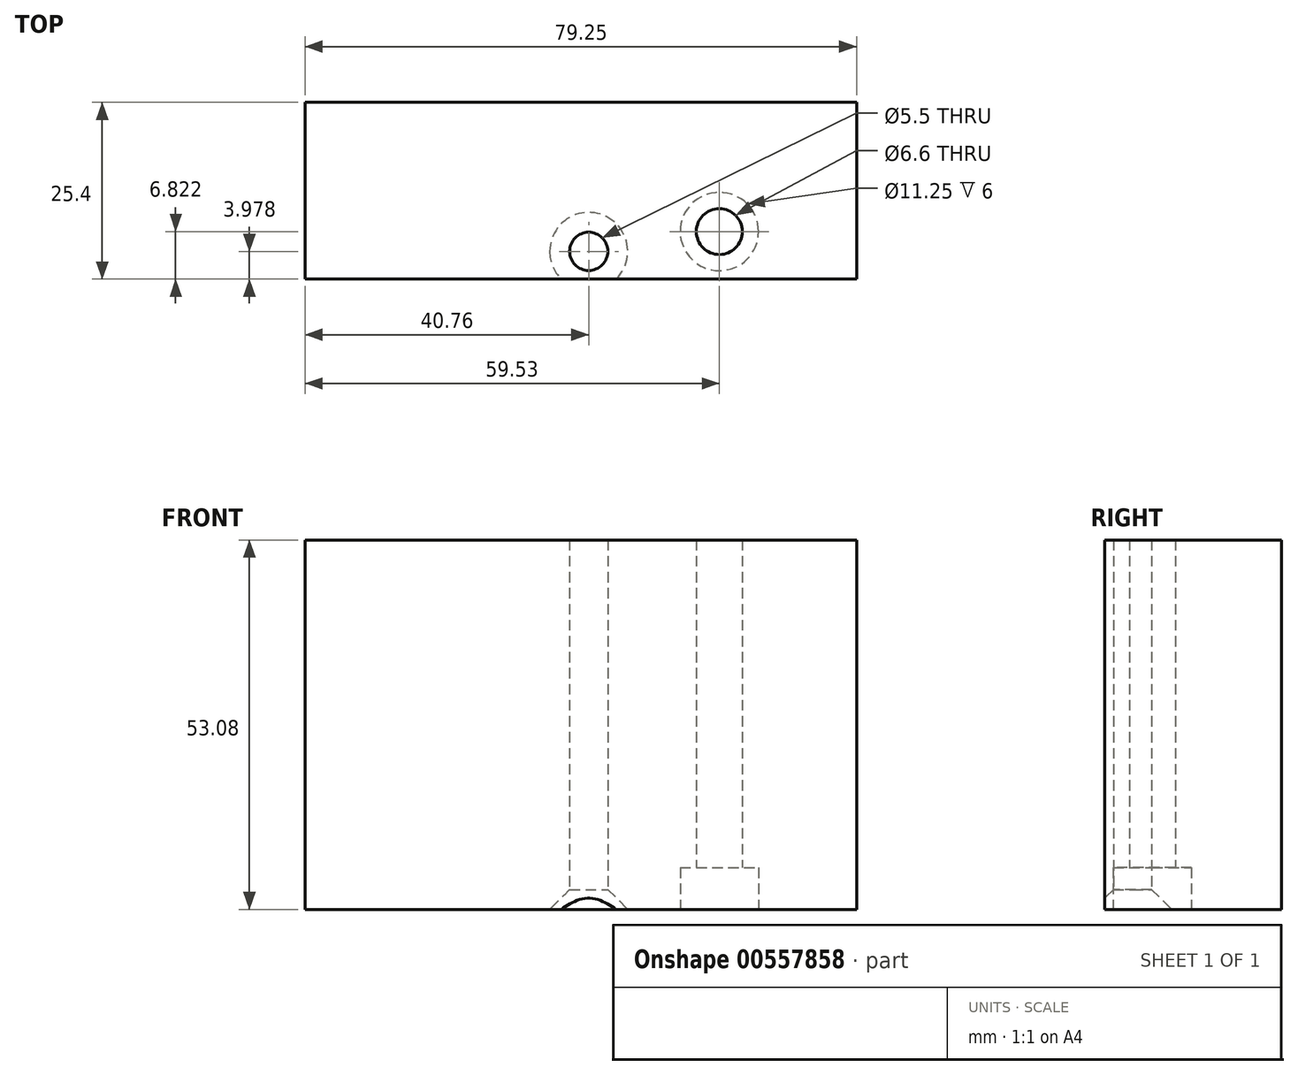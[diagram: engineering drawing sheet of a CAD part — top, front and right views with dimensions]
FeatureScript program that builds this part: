
annotation { "Feature Type Name" : "Feature", "Feature Type Description" : "" }
export const myFeature = defineFeature(function(context is Context, id is Id, definition is map)
    precondition{}
    {
        {
            var Q0;
            Q0=qCreatedBy(makeId("Front.planeOp"),FACE);
            var sketch = newSketch(context, id + "F0", { "sketchPlane" : qUnion([Q0])});
            skLineSegment(sketch, "E0.bottom", {"start": v(-21.8, 17.25) * mm, "end": v(57.45, 17.25) * mm});
            skLineSegment(sketch, "E0.top", {"start": v(-21.8, -35.83) * mm, "end": v(57.45, -35.83) * mm});
            skLineSegment(sketch, "E0.left", {"start": v(-21.8, 17.25) * mm, "end": v(-21.8, -35.83) * mm});
            skLineSegment(sketch, "E0.right", {"start": v(57.45, 17.25) * mm, "end": v(57.45, -35.83) * mm});
            skSolve(sketch);
        }
        {
            var Q0;
            Q0 = qSketchRegion(id + "F0", true);
            extrude(context, id + "F1", {"entities" : qUnion([Q0]), "endBound" : BoundingType.SYMMETRIC, "depth" : 25.4 * mm, "offsetDistance" : 25.4 * mm});
        }
        {
            var Q0;
            Q0=makeQuery(id+"F1.opExtrude","SWEPT_FACE",FACE,{"disambiguationData":[OSD([sQuery(id+"F0.wireOp",EDGE,"E0.top")])]});
            var sketch = newSketch(context, id + "F2", { "sketchPlane" : qUnion([Q0])});
            skLineSegment(sketch, "E1", {"start": v(18.96, 8.72) * mm, "end": v(18.96, 0) * mm});
            skLineSegment(sketch, "E2", {"start": v(13.46, 5.3) * mm, "end": v(36.4, 5.3) * mm});
            skSolve(sketch);
        }
        {
            var Q0;
            Q0=sQuery(id+"F2.wireOp",VERTEX,"E1.start");
            var Q1;
            Q1=makeQuery(id+"F1.opExtrude","SWEPT_BODY",BODY,{"disambiguationData":[OSD([sQuery(id+"F0.wireOp",EDGE,"E0.bottom"),sQuery(id+"F0.wireOp",EDGE,"E0.top"),sQuery(id+"F0.wireOp",EDGE,"E0.left"),sQuery(id+"F0.wireOp",EDGE,"E0.right")])]});
            hole(context, id + "F3", {"style" : HoleStyle.C_SINK, "endStyle" : HoleEndStyle.THROUGH, "standardTappedOrClearance" : lookupTablePath({ "standard" : "ISO", "fit" : "Normal", "size" : "M5", "type" : "Clearance" }), "standardBlindInLast" : lookupTablePath({ "fit" : "Standard", "standard" : "ISO", "size" : "M5", "type" : "Clearance" }), "holeDiameter" : 5.5 * mm, "cSinkDiameter" : 11.2 * mm, "cSinkAngle" : 90 * degree, "isTappedThrough" : true, "tappedDepth" : 12.7 * mm, "tapClearance" : 3, "startFromSketch" : true, "locations" : qUnion([Q0]), "scope" : qUnion([Q1])});
        }
        {
            var Q0;
            Q0=makeQuery(id+"F1.opExtrude","SWEPT_FACE",FACE,{"disambiguationData":[OSD([sQuery(id+"F0.wireOp",EDGE,"E0.top")])]});
            var sketch = newSketch(context, id + "F4", { "sketchPlane" : qUnion([Q0])});
            skPoint(sketch, "E3", {"position": v(37.73, 5.88) * mm});
            skSolve(sketch);
        }
        {
            var Q0;
            Q0=sQuery(id+"F4.wireOp",VERTEX,"E3");
            var Q1;
            Q1=makeQuery(id+"F1.opExtrude","SWEPT_BODY",BODY,{"disambiguationData":[OSD([sQuery(id+"F0.wireOp",EDGE,"E0.bottom"),sQuery(id+"F0.wireOp",EDGE,"E0.top"),sQuery(id+"F0.wireOp",EDGE,"E0.left"),sQuery(id+"F0.wireOp",EDGE,"E0.right")])]});
            hole(context, id + "F5", {"style" : HoleStyle.C_BORE, "endStyle" : HoleEndStyle.THROUGH, "standardTappedOrClearance" : lookupTablePath({ "standard" : "ISO", "fit" : "Normal", "size" : "M6", "type" : "Clearance" }), "standardBlindInLast" : lookupTablePath({ "fit" : "Standard", "standard" : "ISO", "size" : "M6", "type" : "Clearance" }), "holeDiameter" : 6.6 * mm, "cBoreDiameter" : 11.25 * mm, "cBoreDepth" : 6 * mm, "isTappedThrough" : true, "tappedDepth" : 12.7 * mm, "tapClearance" : 3, "startFromSketch" : true, "locations" : qUnion([Q0]), "scope" : qUnion([Q1])});
        }
    });
